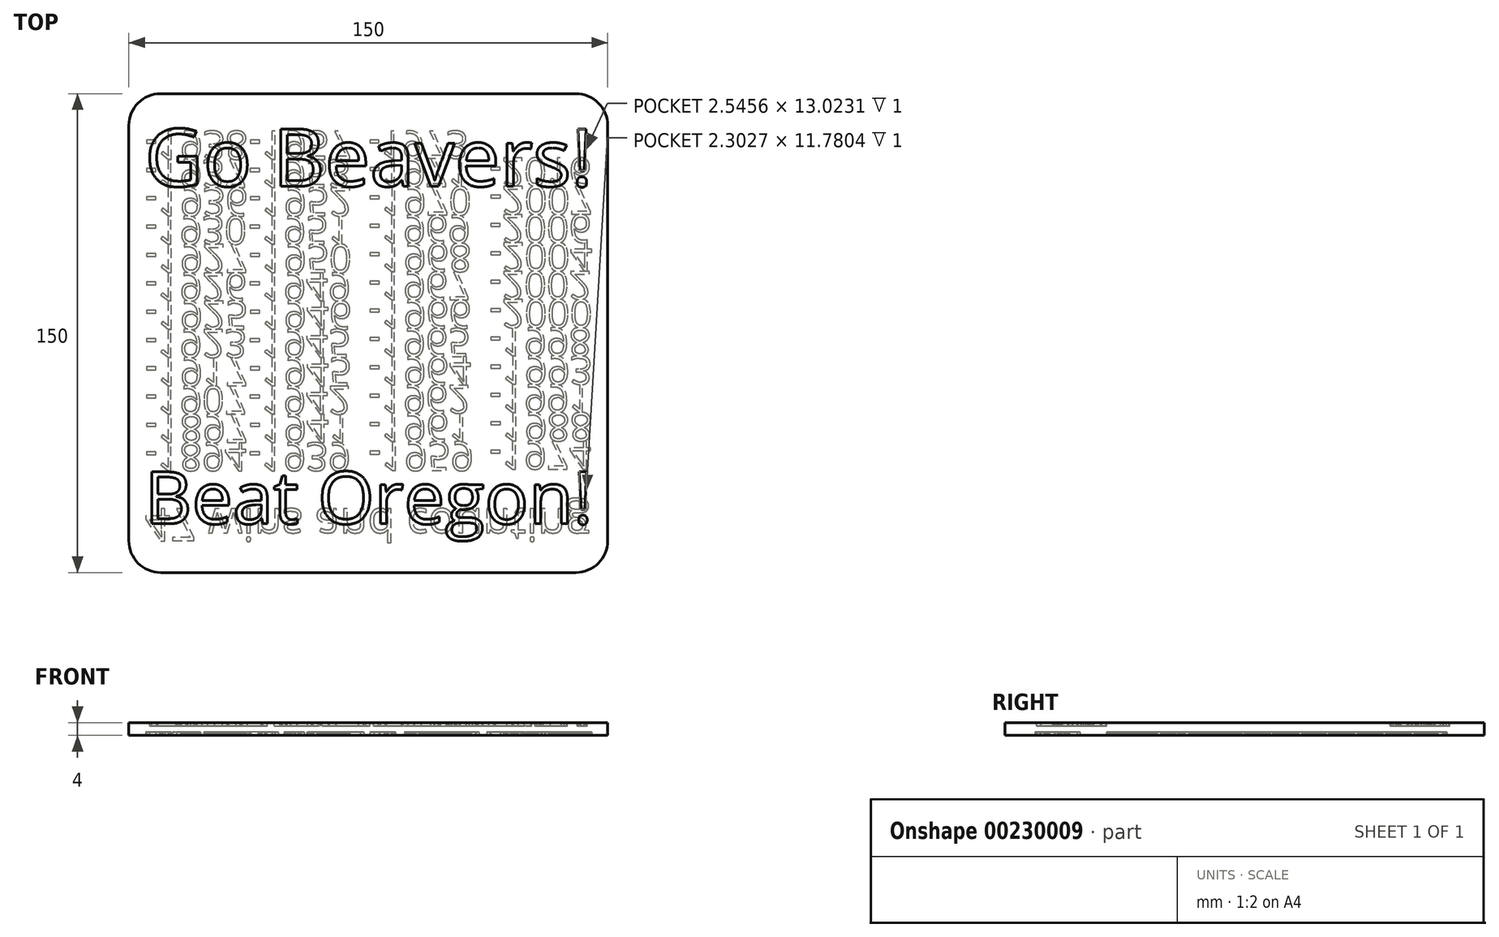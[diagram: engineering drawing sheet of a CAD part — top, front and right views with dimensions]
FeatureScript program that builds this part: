
annotation { "Feature Type Name" : "Feature", "Feature Type Description" : "" }
export const myFeature = defineFeature(function(context is Context, id is Id, definition is map)
    precondition{}
    {
        {
            var Q0;
            Q0=qCreatedBy(makeId("Top.planeOp"),FACE);
            var sketch = newSketch(context, id + "F0", { "sketchPlane" : qUnion([Q0])});
            skLineSegment(sketch, "E0.bottom", {"start": v(75, 75) * mm, "end": v(-75, 75) * mm});
            skLineSegment(sketch, "E0.top", {"start": v(75, -75) * mm, "end": v(-75, -75) * mm});
            skLineSegment(sketch, "E0.left", {"start": v(75, 75) * mm, "end": v(75, -75) * mm});
            skLineSegment(sketch, "E0.right", {"start": v(-75, 75) * mm, "end": v(-75, -75) * mm});
            skPoint(sketch, "E0.middle", {"position": v(0, 0) * mm});
            skSolve(sketch);
        }
        {
            var Q0;
            Q0=makeQuery(id+"F0.imprint","IMPRINT",FACE,{"disambiguationData":[TD([[makeQuery(id+"F0.imprint","IMPRINT",EDGE,{"derivedFrom":sQuery(id+"F0.wireOp",EDGE,"E0.bottom")}),1.0]])]});
            extrude(context, id + "F1", {"entities" : qUnion([Q0]), "depth" : 4 * mm, "symmetric" : true});
        }
        {
            var Q0;
            Q0=makeQuery(id+"F1.opExtrude","SWEPT_EDGE",EDGE,{"disambiguationData":[OSD([sQuery(id+"F0.wireOp",EDGE,"E0.bottom"),sQuery(id+"F0.wireOp",EDGE,"E0.right")])]});
            var Q1;
            Q1=makeQuery(id+"F1.opExtrude","SWEPT_EDGE",EDGE,{"disambiguationData":[OSD([sQuery(id+"F0.wireOp",EDGE,"E0.bottom"),sQuery(id+"F0.wireOp",EDGE,"E0.left")])]});
            var Q2;
            Q2=makeQuery(id+"F1.opExtrude","SWEPT_EDGE",EDGE,{"disambiguationData":[OSD([sQuery(id+"F0.wireOp",EDGE,"E0.top"),sQuery(id+"F0.wireOp",EDGE,"E0.left")])]});
            var Q3;
            Q3=makeQuery(id+"F1.opExtrude","SWEPT_EDGE",EDGE,{"disambiguationData":[OSD([sQuery(id+"F0.wireOp",EDGE,"E0.top"),sQuery(id+"F0.wireOp",EDGE,"E0.right")])]});
            fillet(context, id + "F2", {"entities" : qUnion([Q0, Q1, Q2, Q3]), "radius" : 10 * mm, "tangentPropagation" : true, "allowEdgeOverflow" : false});
        }
        {
            var Q0;
            Q0=makeQuery(id+"F1.opExtrude","CAP_FACE",FACE,{"disambiguationData":[OSD([sQuery(id+"F0.wireOp",EDGE,"E0.bottom"),sQuery(id+"F0.wireOp",EDGE,"E0.top"),sQuery(id+"F0.wireOp",EDGE,"E0.left"),sQuery(id+"F0.wireOp",EDGE,"E0.right")])],"isStart":false});
            var sketch = newSketch(context, id + "F3", { "sketchPlane" : qUnion([Q0])});
            skText(sketch, "E1", { "text": "Go Beavers!", "fontName": "OpenSans-Regular.ttf"});
            skText(sketch, "E2", { "text": "Beat Oregon!", "fontName": "OpenSans-Regular.ttf"});
            const initialGuessF3  = {"E1": [-0.07, 0.04598, 1, 0, 0.01813], "E2": [-0.07, -0.05972, 1, 0, 0.0164]};
            skSetInitialGuess(sketch, initialGuessF3);
            skSolve(sketch);
        }
        {
            var Q0;
            Q0 = qSketchRegion(id + "F3", true);
            extrude(context, id + "F4", {"entities" : qUnion([Q0]), "operationType" : NewBodyOperationType.REMOVE, "oppositeDirection" : true, "depth" : 1 * mm});
        }
        {
            var Q0;
            Q0=makeQuery(id+"F1.opExtrude","CAP_FACE",FACE,{"disambiguationData":[OSD([sQuery(id+"F0.wireOp",EDGE,"E0.bottom"),sQuery(id+"F0.wireOp",EDGE,"E0.top"),sQuery(id+"F0.wireOp",EDGE,"E0.left"),sQuery(id+"F0.wireOp",EDGE,"E0.right")])],"isStart":true});
            var sketch = newSketch(context, id + "F5", { "sketchPlane" : qUnion([Q0])});
            skText(sketch, "E3", { "text": "47 wins and counting", "fontName": "OpenSans-Regular.ttf"});
            skLineSegment(sketch, "E4", {"start": v(0, -75) * mm, "end": v(0, 75) * mm, "construction": true});
            skLineSegment(sketch, "E5", {"start": v(-37.5, -75) * mm, "end": v(-37.5, 75) * mm, "construction": true});
            skLineSegment(sketch, "E6", {"start": v(37.5, -75) * mm, "end": v(37.5, 75) * mm, "construction": true});
            skText(sketch, "E7", { "text": "-1894", "fontName": "OpenSans-Regular.ttf"});
            skText(sketch, "E8", { "text": "-1897", "fontName": "OpenSans-Regular.ttf"});
            skText(sketch, "E9", { "text": "-1907", "fontName": "OpenSans-Regular.ttf"});
            skText(sketch, "E10", { "text": "-1917", "fontName": "OpenSans-Regular.ttf"});
            skText(sketch, "E11", { "text": "-1923", "fontName": "OpenSans-Regular.ttf"});
            skText(sketch, "E12", { "text": "-1925", "fontName": "OpenSans-Regular.ttf"});
            skText(sketch, "E13", { "text": "-1926", "fontName": "OpenSans-Regular.ttf"});
            skText(sketch, "E14", { "text": "-1927", "fontName": "OpenSans-Regular.ttf"});
            skText(sketch, "E15", { "text": "-1930", "fontName": "OpenSans-Regular.ttf"});
            skText(sketch, "E16", { "text": "-1936", "fontName": "OpenSans-Regular.ttf"});
            skText(sketch, "E17", { "text": "-1937", "fontName": "OpenSans-Regular.ttf"});
            skText(sketch, "E18", { "text": "-1938", "fontName": "OpenSans-Regular.ttf"});
            skText(sketch, "E19", { "text": "-1939", "fontName": "OpenSans-Regular.ttf"});
            skText(sketch, "E20", { "text": "-1941", "fontName": "OpenSans-Regular.ttf"});
            skText(sketch, "E21", { "text": "-1942", "fontName": "OpenSans-Regular.ttf"});
            skText(sketch, "E22", { "text": "-1945", "fontName": "OpenSans-Regular.ttf"});
            skText(sketch, "E23", { "text": "-1945", "fontName": "OpenSans-Regular.ttf"});
            skText(sketch, "E24", { "text": "-1946", "fontName": "OpenSans-Regular.ttf"});
            skText(sketch, "E25", { "text": "-1949", "fontName": "OpenSans-Regular.ttf"});
            skText(sketch, "E26", { "text": "-1950", "fontName": "OpenSans-Regular.ttf"});
            skText(sketch, "E27", { "text": "-1951", "fontName": "OpenSans-Regular.ttf"});
            skText(sketch, "E28", { "text": "-1952", "fontName": "OpenSans-Regular.ttf"});
            skText(sketch, "E29", { "text": "-1953", "fontName": "OpenSans-Regular.ttf"});
            skText(sketch, "E30", { "text": "-1957", "fontName": "OpenSans-Regular.ttf"});
            skText(sketch, "E31", { "text": "-1959", "fontName": "OpenSans-Regular.ttf"});
            skText(sketch, "E32", { "text": "-1961", "fontName": "OpenSans-Regular.ttf"});
            skText(sketch, "E33", { "text": "-1962", "fontName": "OpenSans-Regular.ttf"});
            skText(sketch, "E34", { "text": "-1964", "fontName": "OpenSans-Regular.ttf"});
            skText(sketch, "E35", { "text": "-1965", "fontName": "OpenSans-Regular.ttf"});
            skText(sketch, "E36", { "text": "-1966", "fontName": "OpenSans-Regular.ttf"});
            skText(sketch, "E37", { "text": "-1967", "fontName": "OpenSans-Regular.ttf"});
            skText(sketch, "E38", { "text": "-1968", "fontName": "OpenSans-Regular.ttf"});
            skText(sketch, "E39", { "text": "-1969", "fontName": "OpenSans-Regular.ttf"});
            skText(sketch, "E40", { "text": "-1970", "fontName": "OpenSans-Regular.ttf"});
            skText(sketch, "E41", { "text": "-1971", "fontName": "OpenSans-Regular.ttf"});
            skText(sketch, "E42", { "text": "-1973", "fontName": "OpenSans-Regular.ttf"});
            skText(sketch, "E43", { "text": "-1974", "fontName": "OpenSans-Regular.ttf"});
            skText(sketch, "E44", { "text": "-1988", "fontName": "OpenSans-Regular.ttf"});
            skText(sketch, "E45", { "text": "-1991", "fontName": "OpenSans-Regular.ttf"});
            skText(sketch, "E46", { "text": "-1993", "fontName": "OpenSans-Regular.ttf"});
            skText(sketch, "E47", { "text": "-1998", "fontName": "OpenSans-Regular.ttf"});
            skText(sketch, "E48", { "text": "-2000", "fontName": "OpenSans-Regular.ttf"});
            skText(sketch, "E49", { "text": "-2002", "fontName": "OpenSans-Regular.ttf"});
            skText(sketch, "E50", { "text": "-2004", "fontName": "OpenSans-Regular.ttf"});
            skText(sketch, "E51", { "text": "-2006", "fontName": "OpenSans-Regular.ttf"});
            skText(sketch, "E52", { "text": "-2007", "fontName": "OpenSans-Regular.ttf"});
            skText(sketch, "E53", { "text": "-2016", "fontName": "OpenSans-Regular.ttf"});
            const initialGuessF5  = {"E3": [-0.07, 0.055, 1, 0, 0.01014], "E7": [-0.07, 0.03436, 1, 0, 0.00882], "E8": [-0.07, 0.02543, 1, 0, 0.00892], "E9": [-0.07, 0.01661, 1, 0, 0.00882], "E10": [-0.07, 0.0077, 1, 0, 0.00892], "E11": [-0.07, -0.00113, 1, 0, 0.00882], "E12": [-0.07, -0.01005, 1, 0, 0.00892], "E13": [-0.07, -0.01887, 1, 0, 0.00882], "E14": [-0.07, -0.02779, 1, 0, 0.00892], "E15": [-0.07, -0.0366, 1, 0, 0.00882], "E16": [-0.07, -0.04553, 1, 0, 0.00892], "E17": [-0.07, -0.05435, 1, 0, 0.00882], "E18": [-0.07, -0.06327, 1, 0, 0.00892], "E19": [-0.0375, 0.03436, 1, 0, 0.00882], "E20": [-0.0375, 0.02543, 1, 0, 0.00892], "E21": [-0.0375, 0.01661, 1, 0, 0.00882], "E22": [-0.0375, 0.0077, 1, 0, 0.00892], "E23": [-0.0375, -0.00113, 1, 0, 0.00882], "E24": [-0.0375, -0.01005, 1, 0, 0.00892], "E25": [-0.0375, -0.01887, 1, 0, 0.00882], "E26": [-0.0375, -0.02779, 1, 0, 0.00892], "E27": [-0.0375, -0.0366, 1, 0, 0.00882], "E28": [-0.0375, -0.04553, 1, 0, 0.00892], "E29": [-0.0375, -0.05435, 1, 0, 0.00882], "E30": [-0.0375, -0.06327, 1, 0, 0.00892], "E31": [0, 0.03406, 1, 0, 0.00911], "E32": [0, 0.02514, 1, 0, 0.00892], "E33": [0, 0.01632, 1, 0, 0.00882], "E34": [0, 0.0074, 1, 0, 0.00892], "E35": [0, -0.00142, 1, 0, 0.00882], "E36": [0, -0.01034, 1, 0, 0.00892], "E37": [0, -0.01916, 1, 0, 0.00882], "E38": [0, -0.02808, 1, 0, 0.00892], "E39": [0, -0.0369, 1, 0, 0.00882], "E40": [0, -0.04582, 1, 0, 0.00892], "E41": [0, -0.05464, 1, 0, 0.00882], "E42": [0, -0.06327, 1, 0, 0.00863], "E43": [0.0379, 0.03386, 1, 0, 0.00882], "E44": [0.0379, 0.02494, 1, 0, 0.00892], "E45": [0.0379, 0.01612, 1, 0, 0.00882], "E46": [0.0379, 0.0072, 1, 0, 0.00892], "E47": [0.0379, -0.00162, 1, 0, 0.00882], "E48": [0.0379, -0.01054, 1, 0, 0.00892], "E49": [0.0379, -0.01936, 1, 0, 0.00882], "E50": [0.0379, -0.02828, 1, 0, 0.00892], "E51": [0.0379, -0.0371, 1, 0, 0.00882], "E52": [0.0379, -0.04603, 1, 0, 0.00892], "E53": [0.0379, -0.05484, 1, 0, 0.00882]};
            skSetInitialGuess(sketch, initialGuessF5);
            skSolve(sketch);
        }
        {
            var Q0;
            Q0 = qSketchRegion(id + "F5", true);
            extrude(context, id + "F6", {"entities" : qUnion([Q0]), "operationType" : NewBodyOperationType.REMOVE, "oppositeDirection" : true, "depth" : 1 * mm});
        }
    });
